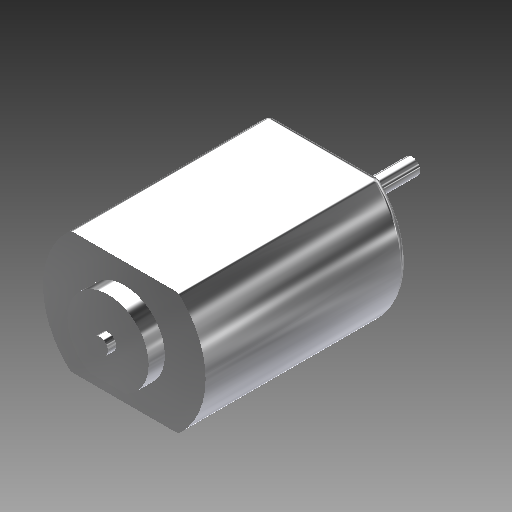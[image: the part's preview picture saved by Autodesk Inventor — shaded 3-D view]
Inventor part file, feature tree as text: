
AUTODESK INVENTOR PART (.ipt)
format: ipt  version: 2017 (Build 210142000, 142)  size: 184,832 bytes
history: native  units: in
note: dims shown in document units (in); Inventor stores cm internally (conversion verified against a paired STEP export)
features: sketch x5, other x3
ambient origin geometry x8: Origin, YZ Plane, XZ Plane, XY Plane, X Axis, Y Axis, Z Axis, Center Point
bodies: Solid1 (feature_tree)
feature tree (8):
  other  "motor_MIR4.ipt"
  other  "Solid1::motor_MIR4.ipt"
  other  "TaggingFeature1"
  sketch  "Sketch1"  dims[d0=0.3937in]
  sketch  "Sketch2"
  sketch  "Sketch3"
  sketch  "Sketch4"
  sketch  "Sketch5"
